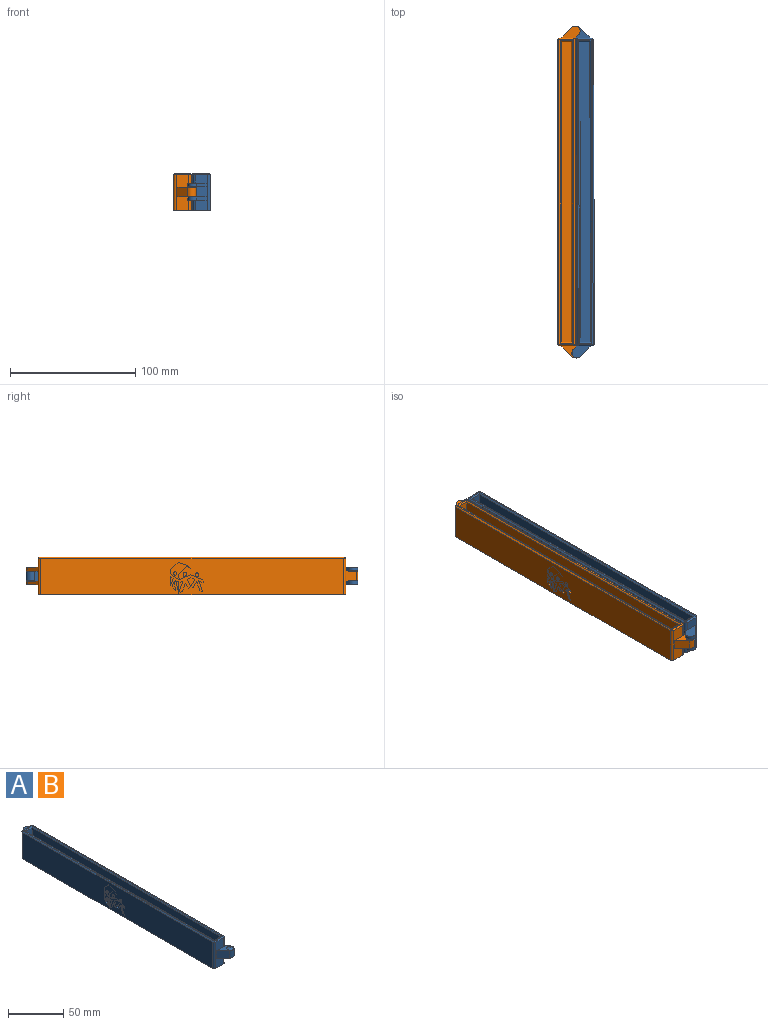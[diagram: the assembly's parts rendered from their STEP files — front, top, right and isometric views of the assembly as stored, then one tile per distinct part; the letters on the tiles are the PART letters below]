
ASSEMBLY  parts=2 mates=1
PART A: 157 faces, bbox 18x265.3x30 mm
  f0: plane 242x29mm, normal (-1,0,0), area 6757mm2, adj f4,f34,f38,f39,f101,f102,f103,f104
  f1: plane 246x29mm, normal (1,0,0), area 6784.6mm2, adj f4,f11,f12,f14,f15,f16,f18,f21
  f2: plane 29x10mm, normal (0,-1,0), area 217.4mm2, adj f4,f22,f23,f24,f35,f38,f40,f44
  f3: plane 29x10mm, normal (0,1,0), area 234.1mm2, adj f4,f12,f13,f14,f16,f17,f18,f36
  f4: plane 246x14mm, normal (0,0,-1), area 3440.6mm2, adj f0,f1,f2,f3,f38,f39,f43,f44
  f5: plane 244x12mm, normal (0,0,1), area 508mm2, adj f30,f31,f32,f33,f34,f35,f36,f37
  f6: plane 240x24mm, normal (-1,0,0), area 5760mm2, adj f7,f9,f10,f32
  f7: plane 240x8mm, normal (0,0,1), area 1920mm2, adj f6,f8,f9,f10
  f8: plane 240x24mm, normal (1,0,0), area 5760mm2, adj f7,f9,f10,f31
  f9: plane 24x8mm, normal (0,1,0), area 192mm2, adj f6,f7,f8,f30
  f10: plane 24x8mm, normal (0,-1,0), area 192mm2, adj f6,f7,f8,f33
  f11: plane 3x2.83mm, normal (0.71,-0.71,0), area 12mm2, adj f1,f12,f14,f28
  f12: plane 15.31x11.66mm, normal (0,0,-1), area 90mm2, adj f1,f3,f11,f13,f28,f43
  f13: plane 8.49x8.49mm, normal (-0.71,0.71,0), area 36mm2, adj f3,f12,f14,f28
  f14: plane 15.31x11.66mm, normal (0,0,1), area 61.7mm2, adj f1,f3,f11,f13,f19,f28,f42
  f15: plane 3x2.83mm, normal (0.71,-0.71,0), area 12mm2, adj f1,f16,f18,f29
  f16: plane 15.31x11.66mm, normal (0,0,-1), area 61.7mm2, adj f1,f3,f15,f17,f20,f29,f42
  f17: plane 8.49x8.49mm, normal (-0.71,0.71,0), area 36mm2, adj f3,f16,f18,f29
  f18: plane 15.31x11.66mm, normal (0,0,1), area 90mm2, adj f1,f3,f15,f17,f29,f41
  f19: cone r=3mm half-angle=71.6deg, axis (0,0,-1), area 29.8mm2, adj f14
  f20: cone r=3mm half-angle=71.6deg, axis (0,0,-1), area 29.8mm2, adj f16
  f21: plane 7.8x2.83mm, normal (0.71,0.71,0), area 31.2mm2, adj f1,f22,f24,f27
  f22: plane 15.31x11.66mm, normal (0,0,1), area 61.7mm2, adj f1,f2,f21,f23,f25,f27,f40
  f23: plane 8.49x8.49mm, normal (-0.71,-0.71,0), area 93.6mm2, adj f2,f22,f24,f27
  f24: plane 15.31x11.66mm, normal (0,0,-1), area 61.7mm2, adj f1,f2,f21,f23,f26,f27,f44
  f25: cone r=3mm half-angle=71.6deg, axis (0,0,-1), area 29.8mm2, adj f22
  f26: cone r=3mm half-angle=71.6deg, axis (0,0,-1), area 29.8mm2, adj f24
  f27: cylinder r=4mm len=7.8mm, axis (0,0,1), area 98mm2, adj f21,f22,f23,f24
  f28: cylinder r=4mm len=6.83mm, axis (0,0,1), area 37.7mm2, adj f11,f12,f13,f14
  f29: cylinder r=4mm len=6.83mm, axis (0,0,1), area 37.7mm2, adj f15,f16,f17,f18
  f30: plane 10x1mm, normal (0,0.71,0.71), area 12.7mm2, adj f5,f9,f31,f32
  f31: plane 242x1mm, normal (0.71,0,0.71), area 340.8mm2, adj f5,f8,f30,f33
  f32: plane 242x1mm, normal (-0.71,0,0.71), area 340.8mm2, adj f5,f6,f30,f33
  f33: plane 10x1mm, normal (0,-0.71,0.71), area 12.7mm2, adj f5,f10,f31,f32
  f34: plane 244.83x1mm, normal (-0.71,0,0.71), area 345.3mm2, adj f0,f5,f35,f36,f38,f39
  f35: plane 12.83x1mm, normal (0,-0.71,0.71), area 17.2mm2, adj f2,f5,f34,f37,f38,f40
  f36: plane 12.83x1mm, normal (0,0.71,0.71), area 17.2mm2, adj f3,f5,f34,f37,f39,f41
  f37: plane 244.83x1mm, normal (0.71,0,0.71), area 345.3mm2, adj f1,f5,f35,f36,f40,f41
  f38: cylinder r=2mm len=29.59mm, axis (0,0,1), area 91.7mm2, adj f0,f2,f4,f34,f35
  f39: cylinder r=2mm len=29.59mm, axis (0,0,1), area 91.7mm2, adj f0,f3,f4,f34,f36
  f40: cylinder r=2mm len=10.69mm, axis (0,0,-1), area 32.4mm2, adj f1,f2,f22,f35,f37
  f41: cylinder r=2mm len=7.59mm, axis (0,0,-1), area 22.6mm2, adj f1,f3,f18,f36,f37
  f42: cylinder r=2mm len=8mm, axis (0,0,-1), area 25.1mm2, adj f1,f3,f14,f16
  f43: cylinder r=2mm len=8mm, axis (0,0,-1), area 25.1mm2, adj f1,f3,f4,f12
  f44: cylinder r=2mm len=11.1mm, axis (0,0,-1), area 34.9mm2, adj f1,f2,f4,f24
  f45: plane 3.14x1.36mm, normal (0,-0.4,0.92), area 2.7mm2, adj f46,f79,f80,f100
  f46: plane 9.51x3.14mm, normal (0,0.95,-0.31), area 8mm2, adj f45,f79,f80,f100
  f47: extruded ~1.68x1mm, area 1.7mm2, adj f48,f77,f80,f81
  f48: extruded ~1.68x0.97mm, area 1.7mm2, adj f47,f49,f80,f81
  f49: extruded ~1.68x1mm, area 1.7mm2, adj f48,f77,f80,f81
  f50: plane 7.25x2.71mm, normal (0,-0.35,-0.94), area 6.2mm2, adj f1,f51,f78,f80
  f51: plane 5.89x5.71mm, normal (0,0.7,-0.72), area 6.6mm2, adj f1,f50,f52,f80
  f52: plane 3.64x0.8mm, normal (0,1,0), area 2.9mm2, adj f1,f51,f53,f80
  f53: plane 6.46x4.57mm, normal (0,0.58,0.82), area 6.3mm2, adj f1,f52,f54,f80
  f54: plane 2.29x0.8mm, normal (0,1,0), area 1.8mm2, adj f1,f53,f55,f80
  f55: plane 2.49x1.8mm, normal (0,-0.59,-0.81), area 2.5mm2, adj f1,f54,f56,f80
  f56: plane 10.33x2.46mm, normal (0,0.97,0.23), area 8.5mm2, adj f1,f55,f57,f80
  f57: plane 3.09x1.54mm, normal (0,-0.45,0.89), area 2.8mm2, adj f1,f56,f58,f80
  f58: plane 6.38x2.2mm, normal (0,-0.95,0.33), area 5.4mm2, adj f1,f57,f59,f80
  f59: plane 3.89x2.25mm, normal (0,0.87,0.5), area 3.6mm2, adj f1,f58,f60,f80
  f60: plane 1.96x1.32mm, normal (0,-0.56,0.83), area 1.9mm2, adj f1,f59,f61,f80
  f61: plane 5.8x2.82mm, normal (0,-0.9,-0.44), area 5.2mm2, adj f1,f60,f62,f80
  f62: plane 3x1.29mm, normal (0,-0.4,0.92), area 2.6mm2, adj f1,f61,f63,f80
  f63: plane 3.11x1.23mm, normal (0,0.37,0.93), area 2.7mm2, adj f1,f62,f64,f80
  f64: plane 5.82x3.18mm, normal (0,0.88,-0.48), area 5.3mm2, adj f1,f63,f65,f80
  f65: plane 2x1.04mm, normal (0,0.46,0.89), area 1.8mm2, adj f1,f64,f66,f80
  f66: plane 4.82x2.79mm, normal (0,-0.87,0.5), area 4.5mm2, adj f1,f65,f67,f80
  f67: plane 7.18x2.54mm, normal (0,0.94,0.33), area 6.1mm2, adj f1,f66,f68,f80
  f68: plane 2.21x1mm, normal (0,0.41,0.91), area 1.9mm2, adj f1,f67,f69,f80
  f69: plane 8.9x3.29mm, normal (0,-0.94,-0.35), area 7.6mm2, adj f1,f68,f70,f80
  f70: plane 3.61x1.53mm, normal (0,0.39,0.92), area 3.1mm2, adj f1,f69,f71,f80
  f71: plane 2.36x0.8mm, normal (0,-1,-0.03), area 1.9mm2, adj f1,f70,f72,f80
  f72: plane 9.86x4.08mm, normal (0,-0.38,-0.92), area 8.5mm2, adj f1,f71,f73,f80
  f73: plane 9.29x3.93mm, normal (0,0.39,-0.92), area 8.1mm2, adj f1,f72,f74,f80
  f74: plane 4.11x0.8mm, normal (0,-1,-0.03), area 3.3mm2, adj f1,f73,f75,f80
  f75: plane 6.64x6.11mm, normal (0,-0.74,0.68), area 7.2mm2, adj f1,f74,f76,f80
  f76: plane 3.29x1.96mm, normal (0,0.51,0.86), area 3.1mm2, adj f1,f75,f78,f80
  f77: extruded ~1.68x0.97mm, area 1.7mm2, adj f47,f49,f80,f81
  f78: plane 2.82x2.36mm, normal (0,-0.64,-0.77), area 2.9mm2, adj f1,f50,f76,f80
  f79: plane 8.15x0.8mm, normal (0,-1,0), area 6.5mm2, adj f45,f46,f80,f100
  f80: plane 25.89x24.75mm, normal (1,0,0), area 214.1mm2, adj f45,f46,f47,f48,f49,f50,f51,f52
  f81: plane 3.36x1.98mm, normal (1,0,0), area 5.2mm2, adj f47,f48,f49,f77
  f82: plane 7.11x1.39mm, normal (0,-0.98,-0.19), area 5.8mm2, adj f1,f83,f84,f85
  f83: plane 4.3x1.57mm, normal (0,0.94,-0.34), area 3.7mm2, adj f1,f82,f84,f85
  f84: plane 2.96x2.8mm, normal (0,0.69,0.73), area 3.3mm2, adj f1,f82,f83,f85
  f85: plane 7.11x2.96mm, normal (1,0,0), area 8.6mm2, adj f82,f83,f84
  f86: plane 1.98x1.52mm, normal (0,-0.61,-0.79), area 2mm2, adj f1,f87,f88,f89
  f87: plane 7.27x0.8mm, normal (0,1,0), area 5.8mm2, adj f1,f86,f88,f89
  f88: plane 5.75x2.02mm, normal (0,-0.94,0.33), area 4.9mm2, adj f1,f86,f87,f89
  f89: plane 7.27x2.02mm, normal (1,0,0), area 7.2mm2, adj f86,f87,f88
  f90: extruded ~1.71x1.05mm, area 1.8mm2, adj f1,f91,f93,f94
  f91: extruded ~1.71x1.39mm, area 1.9mm2, adj f1,f90,f92,f94
  f92: extruded ~1.71x1.05mm, area 1.8mm2, adj f1,f91,f93,f94
  f93: extruded ~1.71x1.39mm, area 1.9mm2, adj f1,f90,f92,f94
  f94: plane 3.43x2.62mm, normal (1,0,0), area 6.5mm2, adj f90,f91,f92,f93
  f95: extruded ~1.71x1.39mm, area 1.9mm2, adj f1,f96,f98,f99
  f96: extruded ~1.71x1.05mm, area 1.8mm2, adj f1,f95,f97,f99
  f97: extruded ~1.71x1.39mm, area 1.9mm2, adj f1,f96,f98,f99
  f98: extruded ~1.71x1.05mm, area 1.8mm2, adj f1,f95,f97,f99
  f99: plane 3.43x2.62mm, normal (1,0,0), area 6.5mm2, adj f95,f96,f97,f98
  f100: plane 9.51x3.14mm, normal (1,0,0), area 12.8mm2, adj f45,f46,f79
  f101: extruded ~1.71x1.05mm, area 1.1mm2, adj f0,f102,f104,f105
  f102: extruded ~1.71x1.39mm, area 1.2mm2, adj f0,f101,f103,f105
  f103: extruded ~1.71x1.05mm, area 1.1mm2, adj f0,f102,f104,f105
  f104: extruded ~1.71x1.39mm, area 1.2mm2, adj f0,f101,f103,f105
  f105: plane 3.43x2.62mm, normal (-1,0,0), area 6.5mm2, adj f101,f102,f103,f104
  f106: plane 3.14x1.36mm, normal (0,0.4,0.92), area 1.7mm2, adj f107,f140,f141,f156
  f107: plane 9.51x3.14mm, normal (0,-0.95,-0.31), area 5mm2, adj f106,f140,f141,f156
  f108: extruded ~1.68x1mm, area 1.1mm2, adj f109,f138,f141,f142
  f109: extruded ~1.68x0.97mm, area 1.1mm2, adj f108,f110,f141,f142
  f110: extruded ~1.68x1mm, area 1.1mm2, adj f109,f138,f141,f142
  f111: plane 7.25x2.71mm, normal (0,0.35,-0.94), area 3.9mm2, adj f0,f112,f139,f141
  f112: plane 5.89x5.71mm, normal (0,-0.7,-0.72), area 4.1mm2, adj f0,f111,f113,f141
  f113: plane 3.64x0.5mm, normal (0,-1,0), area 1.8mm2, adj f0,f112,f114,f141
  f114: plane 6.46x4.57mm, normal (0,-0.58,0.82), area 4mm2, adj f0,f113,f115,f141
  f115: plane 2.29x0.5mm, normal (0,-1,0), area 1.1mm2, adj f0,f114,f116,f141
  f116: plane 2.49x1.8mm, normal (0,0.59,-0.81), area 1.5mm2, adj f0,f115,f117,f141
  f117: plane 10.33x2.46mm, normal (0,-0.97,0.23), area 5.3mm2, adj f0,f116,f118,f141
  f118: plane 3.09x1.54mm, normal (0,0.45,0.89), area 1.7mm2, adj f0,f117,f119,f141
  f119: plane 6.38x2.2mm, normal (0,0.95,0.33), area 3.4mm2, adj f0,f118,f120,f141
  f120: plane 3.89x2.25mm, normal (0,-0.87,0.5), area 2.2mm2, adj f0,f119,f121,f141
  f121: plane 1.96x1.32mm, normal (0,0.56,0.83), area 1.2mm2, adj f0,f120,f122,f141
  f122: plane 5.8x2.82mm, normal (0,0.9,-0.44), area 3.2mm2, adj f0,f121,f123,f141
  f123: plane 3x1.29mm, normal (0,0.4,0.92), area 1.6mm2, adj f0,f122,f124,f141
  f124: plane 3.11x1.23mm, normal (0,-0.37,0.93), area 1.7mm2, adj f0,f123,f125,f141
  f125: plane 5.82x3.18mm, normal (0,-0.88,-0.48), area 3.3mm2, adj f0,f124,f126,f141
  f126: plane 2x1.04mm, normal (0,-0.46,0.89), area 1.1mm2, adj f0,f125,f127,f141
  f127: plane 4.82x2.79mm, normal (0,0.87,0.5), area 2.8mm2, adj f0,f126,f128,f141
  f128: plane 7.18x2.54mm, normal (0,-0.94,0.33), area 3.8mm2, adj f0,f127,f129,f141
  f129: plane 2.21x1mm, normal (0,-0.41,0.91), area 1.2mm2, adj f0,f128,f130,f141
  f130: plane 8.9x3.29mm, normal (0,0.94,-0.35), area 4.7mm2, adj f0,f129,f131,f141
  f131: plane 3.61x1.53mm, normal (0,-0.39,0.92), area 2mm2, adj f0,f130,f132,f141
  f132: plane 2.36x0.5mm, normal (0,1,-0.03), area 1.2mm2, adj f0,f131,f133,f141
  f133: plane 9.86x4.08mm, normal (0,0.38,-0.92), area 5.3mm2, adj f0,f132,f134,f141
  f134: plane 9.29x3.93mm, normal (0,-0.39,-0.92), area 5mm2, adj f0,f133,f135,f141
  f135: plane 4.11x0.5mm, normal (0,1,-0.03), area 2.1mm2, adj f0,f134,f136,f141
  f136: plane 6.64x6.11mm, normal (0,0.74,0.68), area 4.5mm2, adj f0,f135,f137,f141
  f137: plane 3.29x1.96mm, normal (0,-0.51,0.86), area 1.9mm2, adj f0,f136,f139,f141
  f138: extruded ~1.68x0.97mm, area 1.1mm2, adj f108,f110,f141,f142
  f139: plane 2.82x2.36mm, normal (0,0.64,-0.77), area 1.8mm2, adj f0,f111,f137,f141
  f140: plane 8.15x0.5mm, normal (0,1,0), area 4.1mm2, adj f106,f107,f141,f156
  f141: plane 25.89x24.75mm, normal (-1,0,0), area 214.1mm2, adj f106,f107,f108,f109,f110,f111,f112,f113
  f142: plane 3.36x1.98mm, normal (-1,0,0), area 5.2mm2, adj f108,f109,f110,f138
  f143: extruded ~1.71x1.39mm, area 1.2mm2, adj f0,f144,f146,f147
  f144: extruded ~1.71x1.05mm, area 1.1mm2, adj f0,f143,f145,f147
  f145: extruded ~1.71x1.39mm, area 1.2mm2, adj f0,f144,f146,f147
  f146: extruded ~1.71x1.05mm, area 1.1mm2, adj f0,f143,f145,f147
  f147: plane 3.43x2.62mm, normal (-1,0,0), area 6.5mm2, adj f143,f144,f145,f146
  f148: plane 7.11x1.39mm, normal (0,0.98,-0.19), area 3.6mm2, adj f0,f149,f150,f151
  f149: plane 4.3x1.57mm, normal (0,-0.94,-0.34), area 2.3mm2, adj f0,f148,f150,f151
  f150: plane 2.96x2.8mm, normal (0,-0.69,0.73), area 2mm2, adj f0,f148,f149,f151
  f151: plane 7.11x2.96mm, normal (-1,0,0), area 8.6mm2, adj f148,f149,f150
  f152: plane 1.98x1.52mm, normal (0,0.61,-0.79), area 1.2mm2, adj f0,f153,f154,f155
  f153: plane 7.27x0.5mm, normal (0,-1,0), area 3.6mm2, adj f0,f152,f154,f155
  f154: plane 5.75x2.02mm, normal (0,0.94,0.33), area 3mm2, adj f0,f152,f153,f155
  f155: plane 7.27x2.02mm, normal (-1,0,0), area 7.2mm2, adj f152,f153,f154
  f156: plane 9.51x3.14mm, normal (-1,0,0), area 12.8mm2, adj f106,f107,f140
PART B: same geometry as A
PLACE A rot(axis=(0,0,-1),179.8deg) t=(-15.89,-48.18,15.39)mm
PLACE B t=(-30.99,-48.2,15.29)mm fixed
MATE revolute A.f26 <-> B.f19  axis (0,0,-1) through (-23.64,80.81,35.29)mm
